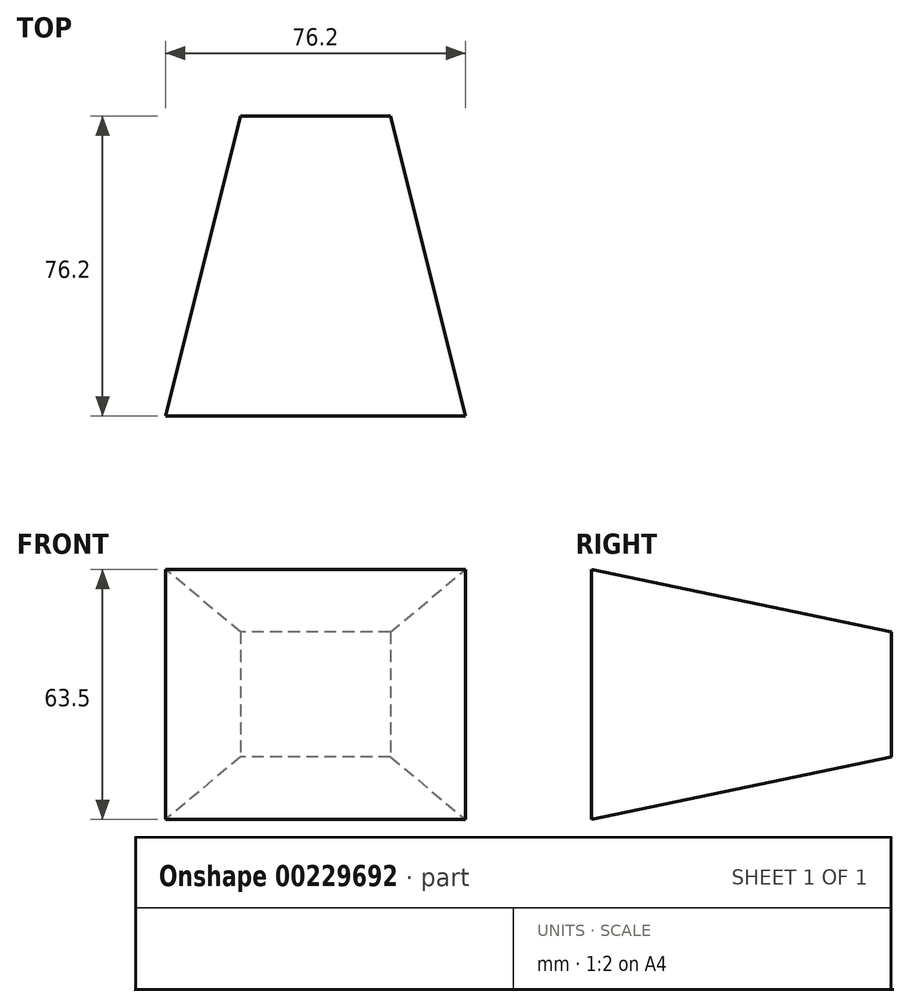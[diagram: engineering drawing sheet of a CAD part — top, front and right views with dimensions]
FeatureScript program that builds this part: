
annotation { "Feature Type Name" : "Feature", "Feature Type Description" : "" }
export const myFeature = defineFeature(function(context is Context, id is Id, definition is map)
    precondition{}
    {
        {
            var Q0;
            Q0=qCreatedBy(makeId("Front.planeOp"),FACE);
            cPlane(context, id + "F0", {"entities" : qUnion([Q0]), "cplaneType" : CPlaneType.OFFSET, "offset" : 76.2 * mm, "width" : 152.4 * mm, "height" : 152.4 * mm});
        }
        {
            var Q0;
            Q0=qCreatedBy(makeId("Front.planeOp"),FACE);
            var sketch = newSketch(context, id + "F1", { "sketchPlane" : qUnion([Q0])});
            skLineSegment(sketch, "E0.bottom", {"start": v(19.05, 15.88) * mm, "end": v(-19.05, 15.88) * mm});
            skLineSegment(sketch, "E0.top", {"start": v(19.05, -15.88) * mm, "end": v(-19.05, -15.88) * mm});
            skLineSegment(sketch, "E0.left", {"start": v(19.05, 15.88) * mm, "end": v(19.05, -15.88) * mm});
            skLineSegment(sketch, "E0.right", {"start": v(-19.05, 15.88) * mm, "end": v(-19.05, -15.88) * mm});
            skPoint(sketch, "E0.middle", {"position": v(0, 0) * mm});
            skSolve(sketch);
        }
        {
            var Q0;
            Q0=qCreatedBy(id+"F0.planeOp",FACE);
            var sketch = newSketch(context, id + "F2", { "sketchPlane" : qUnion([Q0])});
            skLineSegment(sketch, "E1.bottom", {"start": v(38.1, -31.75) * mm, "end": v(-38.1, -31.75) * mm});
            skLineSegment(sketch, "E1.top", {"start": v(38.1, 31.75) * mm, "end": v(-38.1, 31.75) * mm});
            skLineSegment(sketch, "E1.left", {"start": v(38.1, -31.75) * mm, "end": v(38.1, 31.75) * mm});
            skLineSegment(sketch, "E1.right", {"start": v(-38.1, -31.75) * mm, "end": v(-38.1, 31.75) * mm});
            skPoint(sketch, "E1.middle", {"position": v(0, 0) * mm});
            skSolve(sketch);
        }
        {
            var Q0;
            Q0=makeQuery(id+"F1.imprint","IMPRINT",FACE,{"disambiguationData":[TD([[makeQuery(id+"F1.imprint","IMPRINT",EDGE,{"derivedFrom":sQuery(id+"F1.wireOp",EDGE,"E0.bottom")}),1.0]])]});
            var Q1;
            Q1=makeQuery(id+"F2.imprint","IMPRINT",FACE,{"disambiguationData":[TD([[makeQuery(id+"F2.imprint","IMPRINT",EDGE,{"derivedFrom":sQuery(id+"F2.wireOp",EDGE,"E1.bottom")}),-1.0]])]});
            loft(context, id + "F3", {"sheetProfilesArray" : [{ "sheetProfileEntities" : qUnion([Q0]) }, { "sheetProfileEntities" : qUnion([Q1]) }]});
        }
    });
